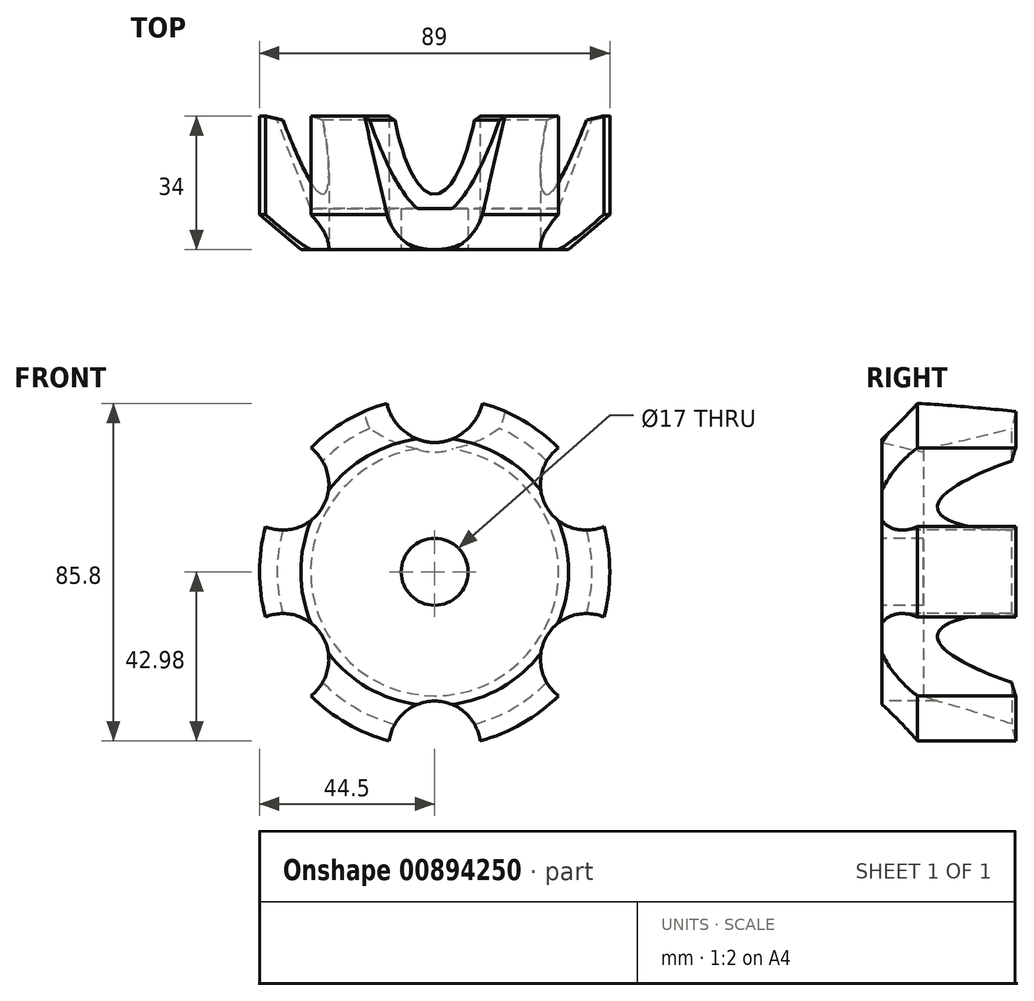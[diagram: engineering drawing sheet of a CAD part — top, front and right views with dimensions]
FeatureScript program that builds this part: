
annotation { "Feature Type Name" : "Feature", "Feature Type Description" : "" }
export const myFeature = defineFeature(function(context is Context, id is Id, definition is map)
    precondition{}
    {
        {
            var Q0;
            Q0=qCreatedBy(makeId("Right.planeOp"),FACE);
            var sketch = newSketch(context, id + "F0", { "sketchPlane" : qUnion([Q0])});
            skLineSegment(sketch, "E0", {"start": v(0, 0) * mm, "end": v(0, 8.5) * mm, "construction": true});
            skLineSegment(sketch, "E1", {"start": v(0, 8.5) * mm, "end": v(0, 34) * mm});
            skLineSegment(sketch, "E2", {"start": v(0, 34) * mm, "end": v(9, 44.5) * mm});
            skLineSegment(sketch, "E3", {"start": v(9, 44.5) * mm, "end": v(34, 44.5) * mm});
            skLineSegment(sketch, "E4", {"start": v(34, 44.5) * mm, "end": v(32.95, 40) * mm});
            skLineSegment(sketch, "E5", {"start": v(32.95, 40) * mm, "end": v(10.5, 31.5) * mm});
            skLineSegment(sketch, "E6", {"start": v(10.5, 8.5) * mm, "end": v(0, 8.5) * mm});
            skLineSegment(sketch, "E7", {"start": v(0, 0) * mm, "end": v(34, 0) * mm});
            skLineSegment(sketch, "E8", {"start": v(10.5, 8.5) * mm, "end": v(10.5, 31.5) * mm});
            skSolve(sketch);
        }
        {
            var Q0;
            Q0 = qSketchRegion(id + "F0", true);
            var Q1;
            Q1=sQuery(id+"F0.wireOp",EDGE,"E7");
            revolve(context, id + "F1", {"surfaceOperationType" : NewSurfaceOperationType.NEW, "entities" : qUnion([Q0]), "axis" : qUnion([Q1]), "revolveType" : RevolveType.FULL});
        }
        {
            var Q0;
            Q0=makeQuery(id+"F1.opRevolve","SWEPT_FACE",FACE,{"disambiguationData":[OSD([sQuery(id+"F0.wireOp",EDGE,"E1")])]});
            var sketch = newSketch(context, id + "F2", { "sketchPlane" : qUnion([Q0])});
            skLineSegment(sketch, "E9", {"start": v(0, 0) * mm, "end": v(0, 44.5) * mm, "construction": true});
            skArc(sketch, "E10", {"start": v(-11.65, 44.5) * mm, "mid": v(0, 32.85) * mm, "end": v(11.65, 44.5) * mm});
            skLineSegment(sketch, "E11", {"start": v(-11.65, 44.5) * mm, "end": v(11.65, 44.5) * mm});
            skArc(sketch, "E12.1.0", {"start": v(-44.36, 12.16) * mm, "mid": v(-28.45, 16.43) * mm, "end": v(-32.71, 32.34) * mm});
            skLineSegment(sketch, "E12.1.1", {"start": v(-44.36, 12.16) * mm, "end": v(-32.71, 32.34) * mm});
            skArc(sketch, "E12.2.0", {"start": v(-32.71, -32.34) * mm, "mid": v(-28.45, -16.42) * mm, "end": v(-44.36, -12.16) * mm});
            skLineSegment(sketch, "E12.2.1", {"start": v(-32.71, -32.34) * mm, "end": v(-44.36, -12.16) * mm});
            skArc(sketch, "E12.3.0", {"start": v(11.65, -44.5) * mm, "mid": v(0, -32.85) * mm, "end": v(-11.65, -44.5) * mm});
            skLineSegment(sketch, "E12.3.1", {"start": v(11.65, -44.5) * mm, "end": v(-11.65, -44.5) * mm});
            skArc(sketch, "E12.4.0", {"start": v(44.36, -12.16) * mm, "mid": v(28.45, -16.43) * mm, "end": v(32.71, -32.34) * mm});
            skLineSegment(sketch, "E12.4.1", {"start": v(44.36, -12.16) * mm, "end": v(32.71, -32.34) * mm});
            skArc(sketch, "E12.5.0", {"start": v(32.71, 32.34) * mm, "mid": v(28.45, 16.42) * mm, "end": v(44.36, 12.16) * mm});
            skLineSegment(sketch, "E12.5.1", {"start": v(32.71, 32.34) * mm, "end": v(44.36, 12.16) * mm});
            skPoint(sketch, "E12.center", {"position": v(0, 0) * mm});
            skSolve(sketch);
        }
        {
            var Q0;
            Q0 = qSketchRegion(id + "F2", true);
            extrude(context, id + "F3", {"entities" : qUnion([Q0]), "operationType" : NewBodyOperationType.REMOVE, "endBound" : BoundingType.THROUGH_ALL, "oppositeDirection" : true, "depth" : 25 * mm, "offsetDistance" : 25 * mm});
        }
        {
            var Q0;
            Q0=qCreatedBy(makeId("Right.planeOp"),FACE);
            var sketch = newSketch(context, id + "F4", { "sketchPlane" : qUnion([Q0])});
            skLineSegment(sketch, "E13", {"start": v(0, 42.85) * mm, "end": v(34, 42.85) * mm});
            skLineSegment(sketch, "E14", {"start": v(0, 42.85) * mm, "end": v(0, 32.85) * mm});
            skLineSegment(sketch, "E15", {"start": v(34, 42.85) * mm, "end": v(34, 24.9) * mm});
            skLineSegment(sketch, "E16", {"start": v(0, 0) * mm, "end": v(0, 32.85) * mm});
            skLineSegment(sketch, "E17", {"start": v(34, 24.9) * mm, "end": v(0, 32.85) * mm});
            skSolve(sketch);
        }
        {
            var Q0;
            Q0 = qSketchRegion(id + "F4", true);
            var Q1;
            Q1=sQuery(id+"F4.wireOp",EDGE,"E13");
            revolve(context, id + "F5", {"operationType" : NewBodyOperationType.REMOVE, "surfaceOperationType" : NewSurfaceOperationType.NEW, "entities" : qUnion([Q0]), "axis" : qUnion([Q1]), "revolveType" : RevolveType.FULL, "oppositeDirection" : true});
        }
    });
